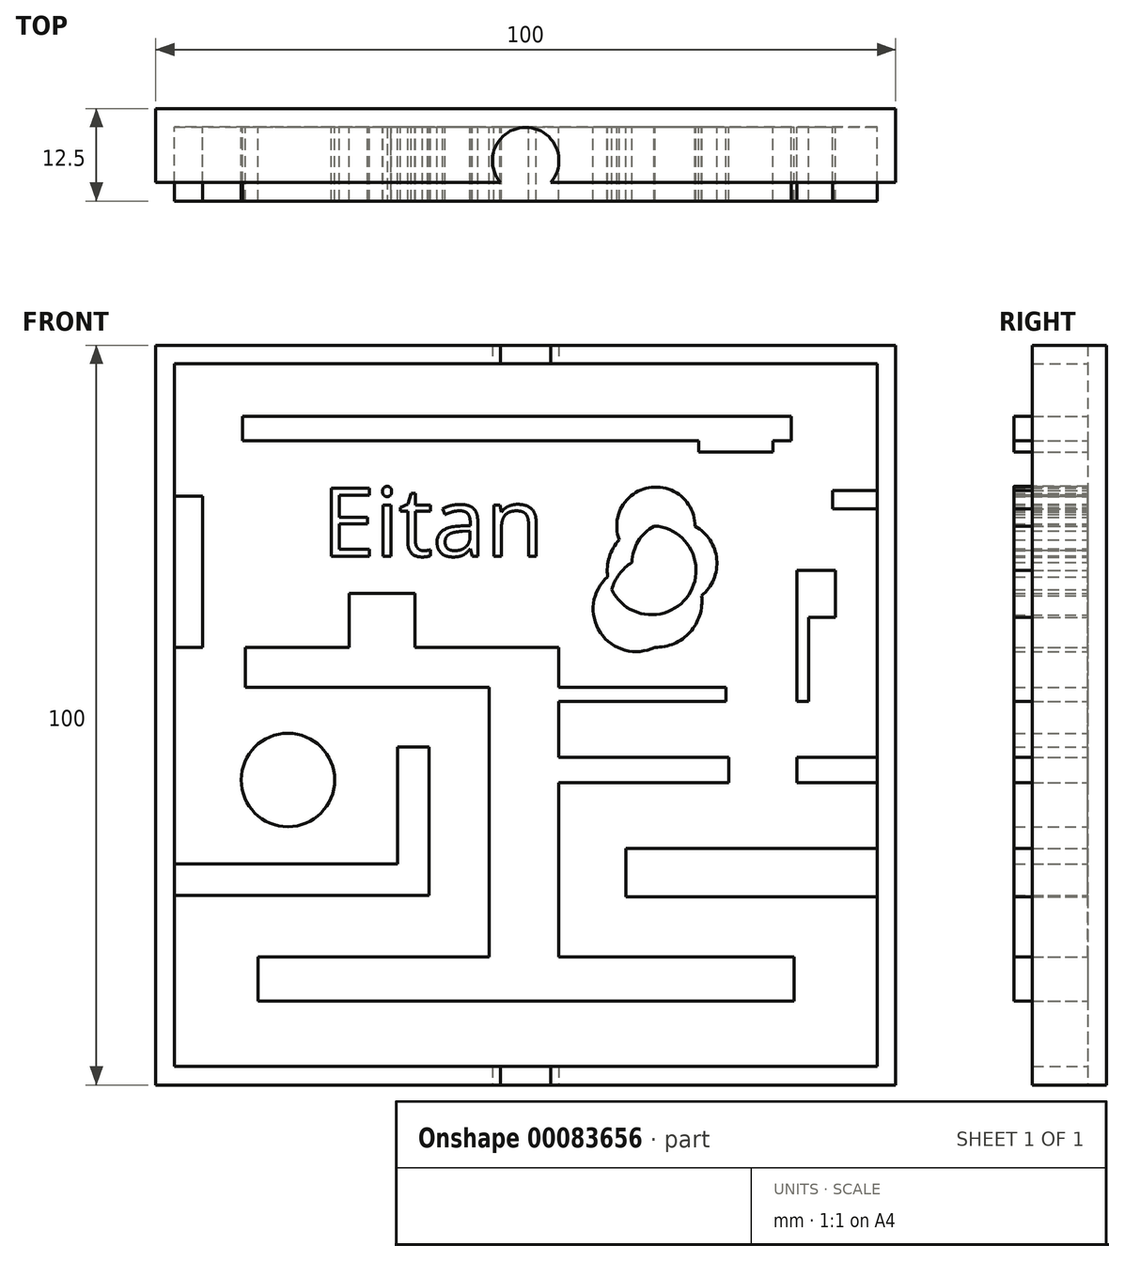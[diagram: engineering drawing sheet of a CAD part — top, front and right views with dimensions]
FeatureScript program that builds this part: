
annotation { "Feature Type Name" : "Feature", "Feature Type Description" : "" }
export const myFeature = defineFeature(function(context is Context, id is Id, definition is map)
    precondition{}
    {
        {
            var Q0;
            Q0=qCreatedBy(makeId("Front.planeOp"),FACE);
            var sketch = newSketch(context, id + "F0", { "sketchPlane" : qUnion([Q0])});
            skLineSegment(sketch, "E0.bottom", {"start": v(50.32, 49.8) * mm, "end": v(-49.68, 49.8) * mm});
            skLineSegment(sketch, "E0.top", {"start": v(50.32, -50.2) * mm, "end": v(-49.68, -50.2) * mm});
            skLineSegment(sketch, "E0.left", {"start": v(50.32, 49.8) * mm, "end": v(50.32, -50.2) * mm});
            skLineSegment(sketch, "E0.right", {"start": v(-49.68, 49.8) * mm, "end": v(-49.68, -50.2) * mm});
            skSolve(sketch);
        }
        {
            var Q0;
            Q0=makeQuery(id+"F0.imprint","IMPRINT",FACE,{"disambiguationData":[TD([[makeQuery(id+"F0.imprint","IMPRINT",EDGE,{"derivedFrom":sQuery(id+"F0.wireOp",EDGE,"E0.bottom")}),1.0]])]});
            extrude(context, id + "F1", {"entities" : qUnion([Q0]), "depth" : 10 * mm});
        }
        {
            var Q0;
            Q0=makeQuery(id+"F1.opExtrude","CAP_FACE",FACE,{"disambiguationData":[OSD([sQuery(id+"F0.wireOp",EDGE,"E0.bottom"),sQuery(id+"F0.wireOp",EDGE,"E0.top"),sQuery(id+"F0.wireOp",EDGE,"E0.left"),sQuery(id+"F0.wireOp",EDGE,"E0.right")])],"isStart":false});
            shell(context, id + "F2", {"entities" : qUnion([Q0]), "thickness" : 2.5 * mm});
        }
        {
            var Q0;
            Q0=makeQuery(id+"F1.opExtrude","SWEPT_FACE",FACE,{"disambiguationData":[OSD([sQuery(id+"F0.wireOp",EDGE,"E0.top")])]});
            var sketch = newSketch(context, id + "F3", { "sketchPlane" : qUnion([Q0])});
            skCircle(sketch, "E1", {"center": v(0.32, 7.04) * mm, "radius": 13.79 * mm});
            skPoint(sketch, "E1.centerSnap0", {"position": v(0.32, 10) * mm});
            skSolve(sketch);
        }
        {
            var Q0;
            Q0=sQuery(id+"F3.wireOp",VERTEX,"E1.center");
            var Q1;
            Q1=makeQuery(id+"F1.opExtrude","SWEPT_BODY",BODY,{"disambiguationData":[OSD([sQuery(id+"F0.wireOp",EDGE,"E0.bottom"),sQuery(id+"F0.wireOp",EDGE,"E0.top"),sQuery(id+"F0.wireOp",EDGE,"E0.left"),sQuery(id+"F0.wireOp",EDGE,"E0.right")])]});
            hole(context, id + "F4", {"style" : HoleStyle.SIMPLE, "endStyle" : HoleEndStyle.THROUGH, "holeDiameter" : 9 * mm, "locations" : qUnion([Q0]), "scope" : qUnion([Q1]), "isTappedThrough" : true});
        }
        {
            var Q0;
            Q0=makeQuery(id+"F2.opShell","OFFSET_FACE",FACE,{"disambiguationData":[OSD([sQuery(id+"F0.wireOp",EDGE,"E0.bottom"),sQuery(id+"F0.wireOp",EDGE,"E0.top"),sQuery(id+"F0.wireOp",EDGE,"E0.left"),sQuery(id+"F0.wireOp",EDGE,"E0.right")])]});
            var sketch = newSketch(context, id + "F5", { "sketchPlane" : qUnion([Q0])});
            skLineSegment(sketch, "E2.bottom", {"start": v(-35.86, -32.87) * mm, "end": v(36.63, -32.87) * mm});
            skLineSegment(sketch, "E2.top", {"start": v(-35.86, -38.84) * mm, "end": v(36.63, -38.84) * mm});
            skLineSegment(sketch, "E2.left", {"start": v(-35.86, -32.87) * mm, "end": v(-35.86, -38.84) * mm});
            skLineSegment(sketch, "E2.right", {"start": v(36.63, -32.87) * mm, "end": v(36.63, -38.84) * mm});
            skLineSegment(sketch, "E3.bottom", {"start": v(-4.63, -32.87) * mm, "end": v(4.82, -32.87) * mm});
            skLineSegment(sketch, "E3.top", {"start": v(-4.63, 0) * mm, "end": v(4.82, 0) * mm});
            skLineSegment(sketch, "E3.left", {"start": v(-4.63, -32.87) * mm, "end": v(-4.63, 0) * mm});
            skLineSegment(sketch, "E3.right", {"start": v(4.82, -32.87) * mm, "end": v(4.82, 0) * mm});
            skLineSegment(sketch, "E4.bottom", {"start": v(-47.18, -24.58) * mm, "end": v(-12.72, -24.58) * mm});
            skLineSegment(sketch, "E4.top", {"start": v(-47.18, -20.34) * mm, "end": v(-12.72, -20.34) * mm});
            skLineSegment(sketch, "E4.left", {"start": v(-47.18, -24.58) * mm, "end": v(-47.18, -20.34) * mm});
            skLineSegment(sketch, "E4.right", {"start": v(-12.72, -24.58) * mm, "end": v(-12.72, -20.34) * mm});
            skLineSegment(sketch, "E5.bottom", {"start": v(-12.72, -20.34) * mm, "end": v(-16.96, -20.34) * mm});
            skLineSegment(sketch, "E5.top", {"start": v(-12.72, -4.53) * mm, "end": v(-16.96, -4.53) * mm});
            skLineSegment(sketch, "E5.left", {"start": v(-12.72, -20.34) * mm, "end": v(-12.72, -4.53) * mm});
            skLineSegment(sketch, "E5.right", {"start": v(-16.96, -20.34) * mm, "end": v(-16.96, -4.53) * mm});
            skLineSegment(sketch, "E6.bottom", {"start": v(4.82, 0) * mm, "end": v(-4.63, 0) * mm});
            skLineSegment(sketch, "E6.top", {"start": v(4.82, 3.57) * mm, "end": v(-4.63, 3.57) * mm});
            skLineSegment(sketch, "E6.left", {"start": v(4.82, 0) * mm, "end": v(4.82, 3.57) * mm});
            skLineSegment(sketch, "E6.right", {"start": v(-4.63, 0) * mm, "end": v(-4.63, 3.57) * mm});
            skLineSegment(sketch, "E7.bottom", {"start": v(-4.82, 3.57) * mm, "end": v(-37.6, 3.57) * mm});
            skLineSegment(sketch, "E7.top", {"start": v(-4.82, 8.96) * mm, "end": v(-37.6, 8.96) * mm});
            skLineSegment(sketch, "E7.left", {"start": v(-4.82, 3.57) * mm, "end": v(-4.82, 8.96) * mm});
            skLineSegment(sketch, "E7.right", {"start": v(-37.6, 3.57) * mm, "end": v(-37.6, 8.96) * mm});
            skLineSegment(sketch, "E8.bottom", {"start": v(-4.82, 8.96) * mm, "end": v(4.82, 8.96) * mm});
            skLineSegment(sketch, "E8.top", {"start": v(-4.82, 3.57) * mm, "end": v(4.82, 3.57) * mm});
            skLineSegment(sketch, "E8.left", {"start": v(-4.82, 8.96) * mm, "end": v(-4.82, 3.57) * mm});
            skLineSegment(sketch, "E8.right", {"start": v(4.82, 8.96) * mm, "end": v(4.82, 3.57) * mm});
            skCircle(sketch, "E9", {"center": v(-31.8, -8.96) * mm, "radius": 6.31 * mm});
            skLineSegment(sketch, "E10.bottom", {"start": v(-37.98, 40.2) * mm, "end": v(36.24, 40.2) * mm});
            skLineSegment(sketch, "E10.top", {"start": v(-37.98, 36.92) * mm, "end": v(36.24, 36.92) * mm});
            skLineSegment(sketch, "E10.left", {"start": v(-37.98, 40.2) * mm, "end": v(-37.98, 36.92) * mm});
            skLineSegment(sketch, "E10.right", {"start": v(36.24, 40.2) * mm, "end": v(36.24, 36.92) * mm});
            skLineSegment(sketch, "E11.bottom", {"start": v(-47.18, 29.4) * mm, "end": v(-43.38, 29.4) * mm});
            skLineSegment(sketch, "E11.top", {"start": v(-47.18, 8.96) * mm, "end": v(-43.38, 8.96) * mm});
            skLineSegment(sketch, "E11.left", {"start": v(-47.18, 29.4) * mm, "end": v(-47.18, 8.96) * mm});
            skLineSegment(sketch, "E11.right", {"start": v(-43.38, 29.4) * mm, "end": v(-43.38, 8.96) * mm});
            skLineSegment(sketch, "E12.bottom", {"start": v(47.82, -18.22) * mm, "end": v(13.88, -18.22) * mm});
            skLineSegment(sketch, "E12.top", {"start": v(47.82, -24.77) * mm, "end": v(13.88, -24.77) * mm});
            skLineSegment(sketch, "E12.left", {"start": v(47.82, -18.22) * mm, "end": v(47.82, -24.77) * mm});
            skLineSegment(sketch, "E12.right", {"start": v(13.88, -18.22) * mm, "end": v(13.88, -24.77) * mm});
            skLineSegment(sketch, "E13.bottom", {"start": v(4.82, -10.5) * mm, "end": v(4.82, -10.5) * mm});
            skLineSegment(sketch, "E13.top", {"start": v(4.82, -5.88) * mm, "end": v(4.82, -5.88) * mm});
            skLineSegment(sketch, "E13.left", {"start": v(4.82, -10.5) * mm, "end": v(4.82, -5.88) * mm});
            skLineSegment(sketch, "E13.right", {"start": v(4.82, -10.5) * mm, "end": v(4.82, -5.88) * mm});
            skLineSegment(sketch, "E14.bottom", {"start": v(4.82, -5.88) * mm, "end": v(27.76, -5.88) * mm});
            skLineSegment(sketch, "E14.top", {"start": v(4.82, -9.35) * mm, "end": v(27.76, -9.35) * mm});
            skLineSegment(sketch, "E14.left", {"start": v(4.82, -5.88) * mm, "end": v(4.82, -9.35) * mm});
            skLineSegment(sketch, "E14.right", {"start": v(27.76, -5.88) * mm, "end": v(27.76, -9.35) * mm});
            skLineSegment(sketch, "E15.bottom", {"start": v(37.01, -5.88) * mm, "end": v(47.82, -5.88) * mm});
            skLineSegment(sketch, "E15.top", {"start": v(37.01, -9.35) * mm, "end": v(47.82, -9.35) * mm});
            skLineSegment(sketch, "E15.left", {"start": v(37.01, -5.88) * mm, "end": v(37.01, -9.35) * mm});
            skLineSegment(sketch, "E15.right", {"start": v(47.82, -5.88) * mm, "end": v(47.82, -9.35) * mm});
            skLineSegment(sketch, "E16.bottom", {"start": v(4.82, 3.57) * mm, "end": v(27.37, 3.57) * mm});
            skLineSegment(sketch, "E16.top", {"start": v(4.82, 1.64) * mm, "end": v(27.37, 1.64) * mm});
            skLineSegment(sketch, "E16.left", {"start": v(4.82, 3.57) * mm, "end": v(4.82, 1.64) * mm});
            skLineSegment(sketch, "E16.right", {"start": v(27.37, 3.57) * mm, "end": v(27.37, 1.64) * mm});
            skLineSegment(sketch, "E17.bottom", {"start": v(37.01, 1.64) * mm, "end": v(38.56, 1.64) * mm});
            skLineSegment(sketch, "E17.top", {"start": v(37.01, 19.37) * mm, "end": v(38.56, 19.37) * mm});
            skLineSegment(sketch, "E17.left", {"start": v(37.01, 1.64) * mm, "end": v(37.01, 19.37) * mm});
            skLineSegment(sketch, "E17.right", {"start": v(38.56, 1.64) * mm, "end": v(38.56, 19.37) * mm});
            skText(sketch, "E18", { "text": "Eitan", "fontName": "OpenSans-Regular.ttf"});
            skLineSegment(sketch, "E19.bottom", {"start": v(-34.12, 29.4) * mm, "end": v(-30.27, 29.4) * mm, "construction": true});
            skLineSegment(sketch, "E19.top", {"start": v(-34.12, 16.29) * mm, "end": v(-30.27, 16.29) * mm, "construction": true});
            skLineSegment(sketch, "E19.left", {"start": v(-34.12, 29.4) * mm, "end": v(-34.12, 16.29) * mm, "construction": true});
            skLineSegment(sketch, "E19.right", {"start": v(-30.27, 29.4) * mm, "end": v(-30.27, 16.29) * mm, "construction": true});
            skCircle(sketch, "E20", {"center": v(20.43, 20.34) * mm, "radius": 5.73 * mm});
            skCircle(sketch, "E21", {"center": v(17.35, 19.37) * mm, "radius": 6 * mm});
            skCircle(sketch, "E22", {"center": v(17.93, 25.35) * mm, "radius": 5.3 * mm});
            skCircle(sketch, "E23", {"center": v(17.95, 15.17) * mm, "radius": 6.2 * mm});
            skCircle(sketch, "E24", {"center": v(15.23, 14.17) * mm, "radius": 5.78 * mm});
            skLineSegment(sketch, "E25.bottom", {"start": v(47.82, 30.17) * mm, "end": v(41.83, 30.17) * mm});
            skLineSegment(sketch, "E25.top", {"start": v(47.82, 27.66) * mm, "end": v(41.83, 27.66) * mm});
            skLineSegment(sketch, "E25.left", {"start": v(47.82, 30.17) * mm, "end": v(47.82, 27.66) * mm});
            skLineSegment(sketch, "E25.right", {"start": v(41.83, 30.17) * mm, "end": v(41.83, 27.66) * mm});
            skLineSegment(sketch, "E26.bottom", {"start": v(-23.52, 8.96) * mm, "end": v(-14.65, 8.96) * mm});
            skLineSegment(sketch, "E26.top", {"start": v(-23.52, 16.29) * mm, "end": v(-14.65, 16.29) * mm});
            skLineSegment(sketch, "E26.left", {"start": v(-23.52, 8.96) * mm, "end": v(-23.52, 16.29) * mm});
            skLineSegment(sketch, "E26.right", {"start": v(-14.65, 8.96) * mm, "end": v(-14.65, 16.29) * mm});
            skLineSegment(sketch, "E27.bottom", {"start": v(23.71, 36.92) * mm, "end": v(33.74, 36.92) * mm});
            skLineSegment(sketch, "E27.top", {"start": v(23.71, 35.37) * mm, "end": v(33.74, 35.37) * mm});
            skLineSegment(sketch, "E27.left", {"start": v(23.71, 36.92) * mm, "end": v(23.71, 35.37) * mm});
            skLineSegment(sketch, "E27.right", {"start": v(33.74, 36.92) * mm, "end": v(33.74, 35.37) * mm});
            const initialGuessF5  = {"E18": [-0.02718, 0.0213, 1, 0, 0.00925]};
            skSetInitialGuess(sketch, initialGuessF5);
            skSolve(sketch);
        }
        {
            var Q0;
            Q0 = qSketchRegion(id + "F5", true);
            extrude(context, id + "F6", {"entities" : qUnion([Q0]), "operationType" : NewBodyOperationType.ADD, "depth" : 10 * mm});
        }
        {
            var Q0;
            {var subQ1=sQuery(id+"F0.wireOp",EDGE,"E0.right");var subQ7=sQuery(id+"F0.wireOp",EDGE,"E0.left");var subQ8=sQuery(id+"F0.wireOp",EDGE,"E0.bottom");var subQ14=sQuery(id+"F0.wireOp",EDGE,"E0.top");Q0=makeQuery(id+"F6.boolean.opBoolean","SPLIT",FACE,{"disambiguationData":[TD([makeQuery(id+"F2.opShell","OFFSET_FACE",FACE,{"disambiguationData":[OSD([subQ8])]})])],"derivedFrom":makeQuery(id+"F2.opShell","OFFSET_FACE",FACE,{"disambiguationData":[OSD([subQ8,subQ14,subQ7,subQ1])]})});}
            var sketch = newSketch(context, id + "F7", { "sketchPlane" : qUnion([Q0])});
            skLineSegment(sketch, "E28.bottom", {"start": v(38.56, 19.37) * mm, "end": v(42.22, 19.37) * mm});
            skLineSegment(sketch, "E28.top", {"start": v(38.56, 13.01) * mm, "end": v(42.22, 13.01) * mm});
            skLineSegment(sketch, "E28.left", {"start": v(38.56, 19.37) * mm, "end": v(38.56, 13.01) * mm});
            skLineSegment(sketch, "E28.right", {"start": v(42.22, 19.37) * mm, "end": v(42.22, 13.01) * mm});
            skSolve(sketch);
        }
        {
            var Q0;
            Q0=makeQuery(id+"F7.imprint","IMPRINT",FACE,{"disambiguationData":[TD([[makeQuery(id+"F7.imprint","IMPRINT",EDGE,{"derivedFrom":sQuery(id+"F7.wireOp",EDGE,"E28.bottom")}),-1.0]])]});
            extrude(context, id + "F8", {"entities" : qUnion([Q0]), "operationType" : NewBodyOperationType.ADD, "depth" : 10 * mm});
        }
    });
